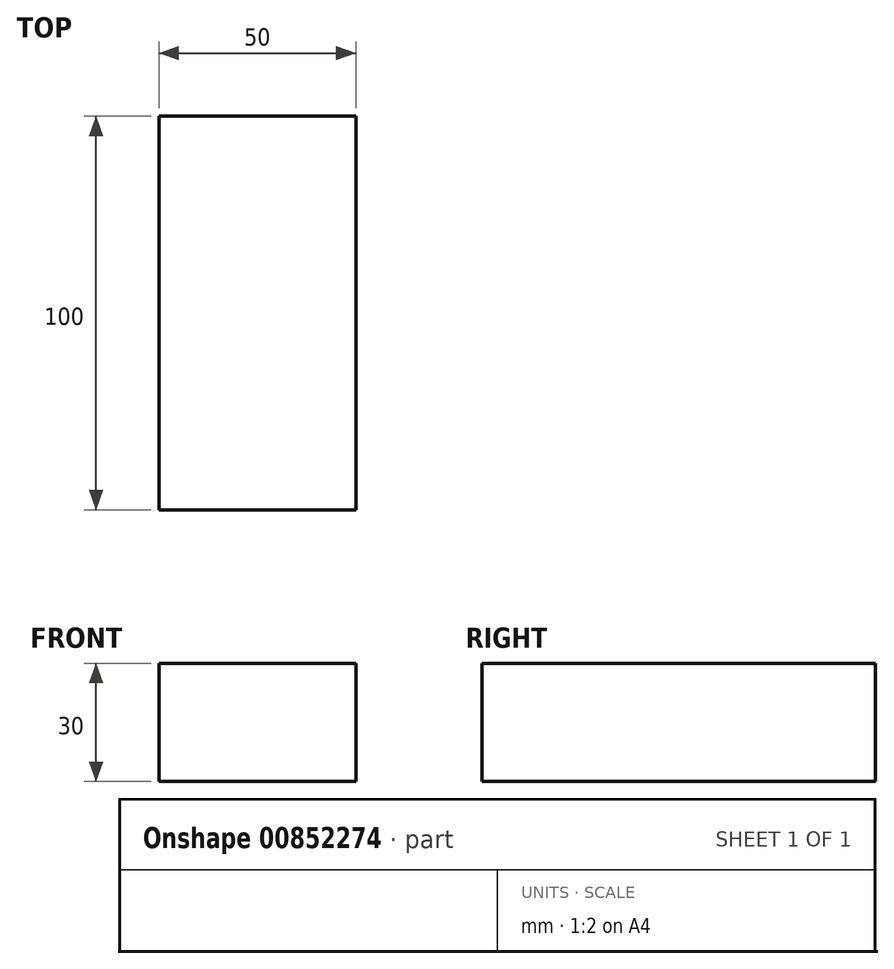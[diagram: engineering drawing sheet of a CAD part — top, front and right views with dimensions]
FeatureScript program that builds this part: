
annotation { "Feature Type Name" : "Feature", "Feature Type Description" : "" }
export const myFeature = defineFeature(function(context is Context, id is Id, definition is map)
    precondition{}
    {
        {
            var Q0;
            Q0=qCreatedBy(makeId("Top.planeOp"),FACE);
            var sketch = newSketch(context, id + "F0", { "sketchPlane" : qUnion([Q0])});
            skLineSegment(sketch, "E0.bottom", {"start": v(25, 50) * mm, "end": v(-25, 50) * mm});
            skLineSegment(sketch, "E0.top", {"start": v(25, -50) * mm, "end": v(-25, -50) * mm});
            skLineSegment(sketch, "E0.left", {"start": v(25, 50) * mm, "end": v(25, -50) * mm});
            skLineSegment(sketch, "E0.right", {"start": v(-25, 50) * mm, "end": v(-25, -50) * mm});
            skPoint(sketch, "E0.middle", {"position": v(0, 0) * mm});
            skSolve(sketch);
        }
        {
            var Q0;
            Q0 = qSketchRegion(id + "F0", true);
            extrude(context, id + "F1", {"entities" : qUnion([Q0]), "depth" : 30 * mm, "offsetDistance" : 25 * mm});
        }
    });
